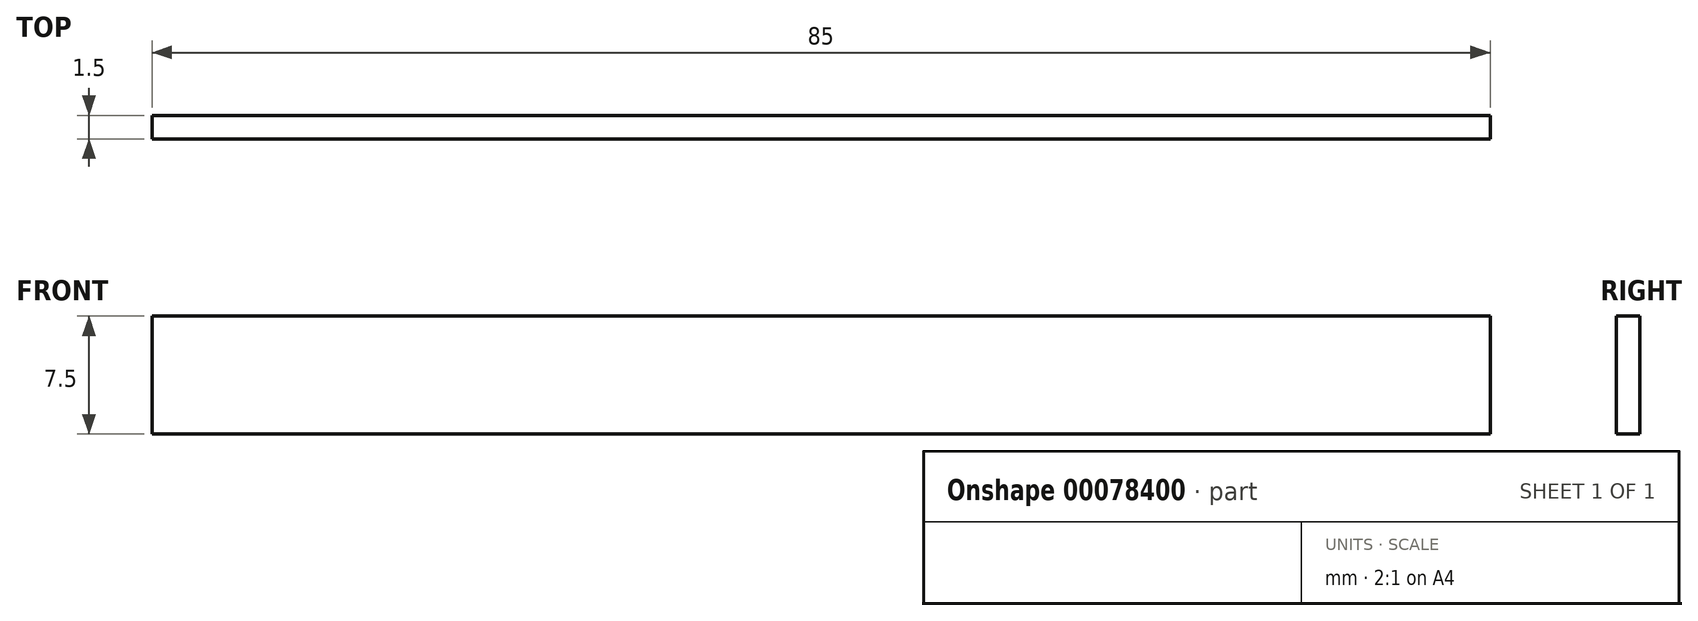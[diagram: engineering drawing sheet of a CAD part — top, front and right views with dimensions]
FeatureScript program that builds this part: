
annotation { "Feature Type Name" : "Feature", "Feature Type Description" : "" }
export const myFeature = defineFeature(function(context is Context, id is Id, definition is map)
    precondition{}
    {
        {
            var Q0;
            Q0=qCreatedBy(makeId("Front.planeOp"),FACE);
            var sketch = newSketch(context, id + "F0", { "sketchPlane" : qUnion([Q0])});
            skLineSegment(sketch, "E0.bottom", {"start": v(-42.5, 3.75) * mm, "end": v(42.5, 3.75) * mm});
            skLineSegment(sketch, "E0.top", {"start": v(-42.5, -3.75) * mm, "end": v(42.5, -3.75) * mm});
            skLineSegment(sketch, "E0.left", {"start": v(-42.5, 3.75) * mm, "end": v(-42.5, -3.75) * mm});
            skLineSegment(sketch, "E0.right", {"start": v(42.5, 3.75) * mm, "end": v(42.5, -3.75) * mm});
            skPoint(sketch, "E0.middle", {"position": v(0, 0) * mm});
            skSolve(sketch);
        }
        {
            var Q0;
            Q0=makeQuery(id+"F0.imprint","IMPRINT",FACE,{"disambiguationData":[TD([[makeQuery(id+"F0.imprint","IMPRINT",EDGE,{"derivedFrom":sQuery(id+"F0.wireOp",EDGE,"E0.bottom")}),-1.0]])]});
            extrude(context, id + "F1", {"entities" : qUnion([Q0]), "depth" : 1.5 * mm, "offsetDistance" : 25 * mm});
        }
    });
